# Revit family: Locker_Cluster
name_source: partatom
category: Casework
units: mm (PartAtom-declared; Revit-internal decimal feet)

## family parameters
Always vertical = Yes
Classification Number = 23.40.20.11.17
Cut with Voids When Loaded = No
Room Calculation Point = No
Shared = No
Work Plane-Based = No

## types (24) — shared parameters
Assembly Code = E2010200
Construction Details = http://www.arcat.com
Default Elevation = 0' - 0"
Equal Sizes = Yes
Finish - Hardware = ARCAT - Steel, Stainless - 28 Ga
Green Building-LEED = http://www.arcat.com
Height = 0' - 0"
Keynote = 10500
Lock Type = 3 Digit Combination, Key Override
Manufacturer = Generic
Manufacturer Fax = (203) 929-2444
Manufacturer Website = http://www.arcat.com
Material - Frame Components = ARCAT - Steel - 18 Ga
Material - Locker Door = ARCAT - Steel - 22 Ga
Model = Generic
Number = 103
Numbered = Yes
Product Data = http://www.arcat.com
Product Properties = http://www.arcat.com
Specification = http://www.arcat.com
zero-valued in all types: Expected Lifespan (Years), Maintenance Schedule (Months), Storage Volume, Warranty Duration (Years)

## per-type parameters (varying)
| type | Depth | Description | Door Width | Width |
| 3 Tier 12x12x7-0 | 1' - 0" | 12x12x7-0 Storage Locker Cluster | 0' - 10" | 1' - 0" |
| 3 Tier 12x16x7-0 | 1' - 0" | 12x16x7-0 Storage Locker Cluster | 1' - 2" | 1' - 4" |
| 3 Tier 12x24x7-0 | 1' - 0" | 12x24x7-0 Storage Locker Cluster | 1' - 10" | 2' - 0" |
| 3 Tier 16x12x7-0 | 1' - 4" | 16x12x7-0 Storage Locker Cluster | 0' - 10" | 1' - 0" |
| 3 Tier 16x16x7-0 | 1' - 4" | 16x16x7-0 Storage Locker Cluster | 1' - 2" | 1' - 4" |
| 3 Tier 16x24x7-0 | 1' - 4" | 16x24x7-0 Storage Locker Cluster | 1' - 10" | 2' - 0" |
| 3 Tier 16x24x8-0 | 1' - 4" | 16x24x8-0 Storage Locker Cluster | 1' - 10" | 2' - 0" |
| 3 Tier 16x24x6-0 | 1' - 4" | 16x24x6-0 Storage Locker Cluster | 1' - 10" | 2' - 0" |
| 3 Tier 16x24x7-6 | 1' - 4" | 16x24x7-6 Storage Locker Cluster | 1' - 10" | 2' - 0" |
| 3 Tier 16x16x8-0 | 1' - 4" | 16x16x8-0 Storage Locker Cluster | 1' - 2" | 1' - 4" |
| 3 Tier 16x16x6-0 | 1' - 4" | 16x16x6-0 Storage Locker Cluster | 1' - 2" | 1' - 4" |
| 3 Tier 16x16x7-6 | 1' - 4" | 16x16x7-6 Storage Locker Cluster | 1' - 2" | 1' - 4" |
| 3 Tier 16x12x8-0 | 1' - 4" | 16x12x8-0 Storage Locker Cluster | 0' - 10" | 1' - 0" |
| 3 Tier 16x12x6-0 | 1' - 4" | 16x12x6-0 Storage Locker Cluster | 0' - 10" | 1' - 0" |
| 3 Tier 16x12x7-6 | 1' - 4" | 16x12x7-6 Storage Locker Cluster | 0' - 10" | 1' - 0" |
| 3 Tier 12x24x8-0 | 1' - 0" | 12x24x8-0 Storage Locker Cluster | 1' - 10" | 2' - 0" |
| 3 Tier 12x24x6-0 | 1' - 0" | 12x24x6-0 Storage Locker Cluster | 1' - 10" | 2' - 0" |
| 3 Tier 12x24x7-6 | 1' - 0" | 12x24x7-6 Storage Locker Cluster | 1' - 10" | 2' - 0" |
| 3 Tier 12x16x8-0 | 1' - 0" | 12x16x8-0 Storage Locker Cluster | 1' - 2" | 1' - 4" |
| 3 Tier 12x16x6-0 | 1' - 0" | 12x16x6-0 Storage Locker Cluster | 1' - 2" | 1' - 4" |
| 3 Tier 12x16x7-6 | 1' - 0" | 12x16x7-6 Storage Locker Cluster | 1' - 2" | 1' - 4" |
| 3 Tier 12x12x8-0 | 1' - 0" | 12x12x8-0 Storage Locker Cluster | 0' - 10" | 1' - 0" |
| 3 Tier 12x12x6-0 | 1' - 0" | 12x12x6-0 Storage Locker Cluster | 0' - 10" | 1' - 0" |
| 3 Tier 12x12x7-6 | 1' - 0" | 12x12x7-6 Storage Locker Cluster | 0' - 10" | 1' - 0" |

## geometry (parser evidence)
native form markers: Sweep x3
no freeform markers — native parametric forms only
